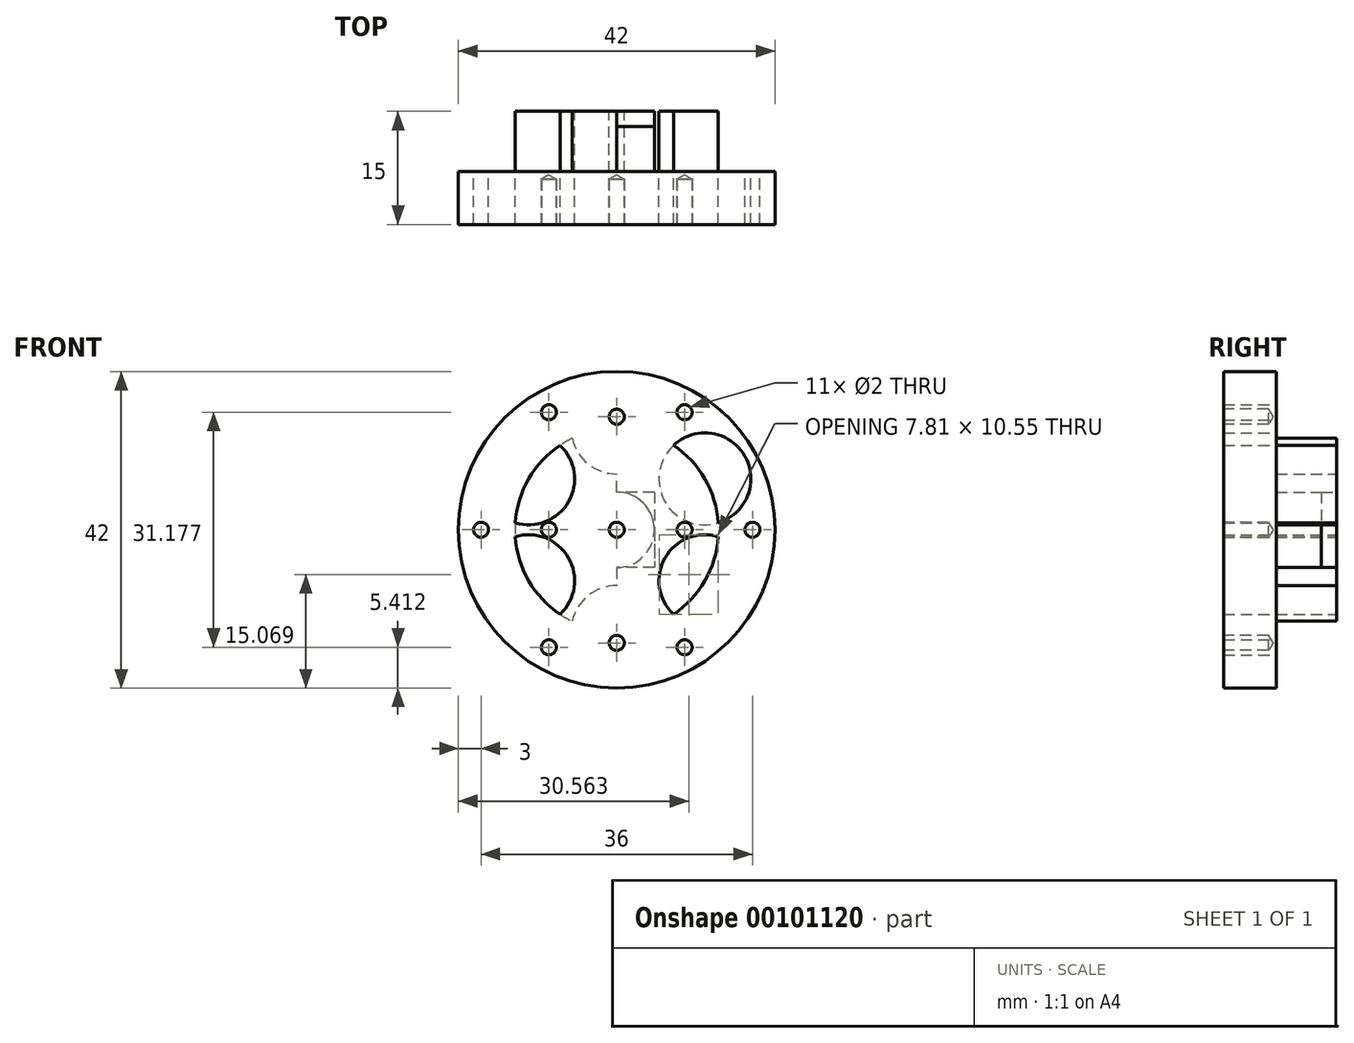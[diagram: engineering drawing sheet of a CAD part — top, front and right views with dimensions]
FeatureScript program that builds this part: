
annotation { "Feature Type Name" : "Feature", "Feature Type Description" : "" }
export const myFeature = defineFeature(function(context is Context, id is Id, definition is map)
    precondition{}
    {
        {
            var Q0;
            Q0=qCreatedBy(makeId("Front.planeOp"),FACE);
            var sketch = newSketch(context, id + "F0", { "sketchPlane" : qUnion([Q0])});
            skCircle(sketch, "E0", {"center": v(0, 0) * mm, "radius": 21 * mm});
            skCircle(sketch, "E1", {"center": v(0, 0) * mm, "radius": 13.5 * mm});
            skCircle(sketch, "E2", {"center": v(0, 13.5) * mm, "radius": 6.1 * mm});
            skLineSegment(sketch, "E3", {"start": v(0, 0) * mm, "end": v(0, 13.5) * mm});
            skLineSegment(sketch, "E4.3.0", {"start": v(0, 0) * mm, "end": v(0, -17.5) * mm});
            skCircle(sketch, "E5", {"center": v(0, 0) * mm, "radius": 5 * mm});
            skCircle(sketch, "E6.1.0", {"center": v(-11.7, 6.75) * mm, "radius": 6.1 * mm});
            skCircle(sketch, "E6.2.0", {"center": v(-11.7, -6.75) * mm, "radius": 6.1 * mm});
            skCircle(sketch, "E6.3.0", {"center": v(0, -13.5) * mm, "radius": 6.1 * mm});
            skCircle(sketch, "E6.4.0", {"center": v(11.7, -6.75) * mm, "radius": 6.1 * mm});
            skCircle(sketch, "E6.5.0", {"center": v(11.7, 6.75) * mm, "radius": 6.1 * mm});
            skSolve(sketch);
        }
        {
            var Q0;
            Q0=qSketchRegion(id+"F0",true);
            var Q1;
            {var subQ3=sQuery(id+"F0.wireOp",EDGE,"tZOFWktZ-ElV9-8rvC-aUia-Pu95TyRWtfmy");var subQ5=sQuery(id+"F0.wireOp",EDGE,"E1");var subQ6=makeQuery(id+"F0.imprint","INTERSECT",VERTEX,{"disambiguationData":[OD(1.0)],"derivedFrom":[subQ5,subQ3]});Q1=makeQuery(id+"F0.imprint","IMPRINT",FACE,{"disambiguationData":[TD([[makeQuery(id+"F0.imprint","IMPRINT",EDGE,{"disambiguationData":[TD([[subQ6,-1.0]])],"derivedFrom":subQ5}),1.0]])]});}
            var Q2;
            {var subQ3=sQuery(id+"F0.wireOp",EDGE,"KCc62wJ9-mbiY-6kxt-bQFC-ecyapfwqHlXu");var subQ5=sQuery(id+"F0.wireOp",EDGE,"E1");var subQ6=makeQuery(id+"F0.imprint","INTERSECT",VERTEX,{"disambiguationData":[OD(1.0)],"derivedFrom":[subQ5,subQ3]});Q2=makeQuery(id+"F0.imprint","IMPRINT",FACE,{"disambiguationData":[TD([[makeQuery(id+"F0.imprint","IMPRINT",EDGE,{"disambiguationData":[TD([[subQ6,-1.0]])],"derivedFrom":subQ5}),1.0]])]});}
            var Q3;
            {var subQ3=sQuery(id+"F0.wireOp",EDGE,"0Yy4USeo-LOO3-cS4v-iVgx-1SsoAEMeRNpn");var subQ5=sQuery(id+"F0.wireOp",EDGE,"E1");var subQ6=makeQuery(id+"F0.imprint","INTERSECT",VERTEX,{"disambiguationData":[OD(1.0)],"derivedFrom":[subQ5,subQ3]});Q3=makeQuery(id+"F0.imprint","IMPRINT",FACE,{"disambiguationData":[TD([[makeQuery(id+"F0.imprint","IMPRINT",EDGE,{"disambiguationData":[TD([[subQ6,-1.0]])],"derivedFrom":subQ5}),1.0]])]});}
            var Q4;
            {var subQ5=sQuery(id+"F0.wireOp",EDGE,"E1");var subQ7=sQuery(id+"F0.wireOp",EDGE,"54YZh0VT-RaSH-f3J3-LX5H-yRfJ3TOlvn7D");var subQ8=makeQuery(id+"F0.imprint","INTERSECT",VERTEX,{"disambiguationData":[OD(0.0)],"derivedFrom":[subQ5,subQ7]});Q4=makeQuery(id+"F0.imprint","IMPRINT",FACE,{"disambiguationData":[TD([[makeQuery(id+"F0.imprint","IMPRINT",EDGE,{"disambiguationData":[TD([[subQ8,-1.0]])],"derivedFrom":subQ5}),1.0]])]});}
            var Q5;
            {var subQ3=sQuery(id+"F0.wireOp",EDGE,"E2");var subQ6=sQuery(id+"F0.wireOp",EDGE,"E1");var subQ9=makeQuery(id+"F0.imprint","INTERSECT",VERTEX,{"disambiguationData":[OD(1.0)],"derivedFrom":[subQ6,subQ3]});Q5=makeQuery(id+"F0.imprint","IMPRINT",FACE,{"disambiguationData":[TD([[makeQuery(id+"F0.imprint","IMPRINT",EDGE,{"disambiguationData":[TD([[subQ9,-1.0]])],"derivedFrom":subQ6}),1.0]])]});}
            var Q6;
            {var subQ0=sQuery(id+"F0.wireOp",EDGE,"E1");var subQ1=makeQuery(id+"F0.imprint","INTERSECT",VERTEX,{"derivedFrom":[subQ0,sQuery(id+"F0.wireOp",EDGE,"E4.3.0")]});Q6=makeQuery(id+"F0.imprint","IMPRINT",FACE,{"disambiguationData":[TD([[makeQuery(id+"F0.imprint","IMPRINT",EDGE,{"disambiguationData":[TD([[subQ1,1.0]])],"derivedFrom":subQ0}),-1.0]])]});}
            var Q7;
            {var subQ0=sQuery(id+"F0.wireOp",EDGE,"E4.3.0");var subQ1=sQuery(id+"F0.wireOp",EDGE,"E1");var subQ2=makeQuery(id+"F0.imprint","INTERSECT",VERTEX,{"derivedFrom":[subQ1,subQ0]});Q7=makeQuery(id+"F0.imprint","IMPRINT",FACE,{"disambiguationData":[TD([[makeQuery(id+"F0.imprint","IMPRINT",EDGE,{"disambiguationData":[TD([[subQ2,-1.0]])],"derivedFrom":subQ1}),1.0]])]});}
            var Q8;
            {var subQ0=sQuery(id+"F0.wireOp",EDGE,"E4.3.0");var subQ1=sQuery(id+"F0.wireOp",EDGE,"E1");var subQ2=makeQuery(id+"F0.imprint","INTERSECT",VERTEX,{"derivedFrom":[subQ1,subQ0]});Q8=makeQuery(id+"F0.imprint","IMPRINT",FACE,{"disambiguationData":[TD([[makeQuery(id+"F0.imprint","IMPRINT",EDGE,{"disambiguationData":[TD([[subQ2,1.0]])],"derivedFrom":subQ1}),1.0]])]});}
            var Q9;
            {var subQ0=sQuery(id+"F0.wireOp",EDGE,"E6.4.0");var subQ1=sQuery(id+"F0.wireOp",EDGE,"E1");var subQ2=makeQuery(id+"F0.imprint","INTERSECT",VERTEX,{"disambiguationData":[OD(0.0)],"derivedFrom":[subQ1,subQ0]});Q9=makeQuery(id+"F0.imprint","IMPRINT",FACE,{"disambiguationData":[TD([[makeQuery(id+"F0.imprint","IMPRINT",EDGE,{"disambiguationData":[TD([[subQ2,-1.0]])],"derivedFrom":subQ1}),-1.0]])]});}
            var Q10;
            {var subQ0=sQuery(id+"F0.wireOp",EDGE,"E6.5.0");var subQ1=sQuery(id+"F0.wireOp",EDGE,"E1");var subQ16=makeQuery(id+"F0.imprint","INTERSECT",VERTEX,{"disambiguationData":[OD(0.0)],"derivedFrom":[subQ1,subQ0]});Q10=makeQuery(id+"F0.imprint","IMPRINT",FACE,{"disambiguationData":[TD([[makeQuery(id+"F0.imprint","IMPRINT",EDGE,{"disambiguationData":[TD([[subQ16,-1.0]])],"derivedFrom":subQ1}),1.0]])]});}
            var Q11;
            {var subQ0=sQuery(id+"F0.wireOp",EDGE,"E4.3.0");var subQ1=sQuery(id+"F0.wireOp",EDGE,"E3");var subQ2=makeQuery(id+"F0.imprint","INTERSECT",VERTEX,{"derivedFrom":[subQ1,subQ0]});Q11=makeQuery(id+"F0.imprint","IMPRINT",FACE,{"disambiguationData":[TD([[makeQuery(id+"F0.imprint","IMPRINT",EDGE,{"disambiguationData":[TD([[subQ2,-1.0]])],"derivedFrom":subQ1}),-1.0]])]});}
            var Q12;
            {var subQ0=sQuery(id+"F0.wireOp",EDGE,"E4.3.0");var subQ1=sQuery(id+"F0.wireOp",EDGE,"E3");var subQ2=makeQuery(id+"F0.imprint","INTERSECT",VERTEX,{"derivedFrom":[subQ1,subQ0]});Q12=makeQuery(id+"F0.imprint","IMPRINT",FACE,{"disambiguationData":[TD([[makeQuery(id+"F0.imprint","IMPRINT",EDGE,{"disambiguationData":[TD([[subQ2,-1.0]])],"derivedFrom":subQ1}),1.0]])]});}
            var Q13;
            {var subQ0=sQuery(id+"F0.wireOp",EDGE,"E6.2.0");var subQ1=sQuery(id+"F0.wireOp",EDGE,"E1");var subQ2=makeQuery(id+"F0.imprint","INTERSECT",VERTEX,{"disambiguationData":[OD(0.0)],"derivedFrom":[subQ1,subQ0]});Q13=makeQuery(id+"F0.imprint","IMPRINT",FACE,{"disambiguationData":[TD([[makeQuery(id+"F0.imprint","IMPRINT",EDGE,{"disambiguationData":[TD([[subQ2,-1.0]])],"derivedFrom":subQ1}),-1.0]])]});}
            var Q14;
            {var subQ0=sQuery(id+"F0.wireOp",EDGE,"E6.1.0");var subQ1=sQuery(id+"F0.wireOp",EDGE,"E1");var subQ2=makeQuery(id+"F0.imprint","INTERSECT",VERTEX,{"disambiguationData":[OD(0.0)],"derivedFrom":[subQ1,subQ0]});Q14=makeQuery(id+"F0.imprint","IMPRINT",FACE,{"disambiguationData":[TD([[makeQuery(id+"F0.imprint","IMPRINT",EDGE,{"disambiguationData":[TD([[subQ2,-1.0]])],"derivedFrom":subQ1}),-1.0]])]});}
            var Q15;
            {var subQ0=sQuery(id+"F0.wireOp",EDGE,"E1");var subQ1=makeQuery(id+"F0.imprint","INTERSECT",VERTEX,{"derivedFrom":[subQ0,sQuery(id+"F0.wireOp",EDGE,"E3")]});Q15=makeQuery(id+"F0.imprint","IMPRINT",FACE,{"disambiguationData":[TD([[makeQuery(id+"F0.imprint","IMPRINT",EDGE,{"disambiguationData":[TD([[subQ1,1.0]])],"derivedFrom":subQ0}),-1.0]])]});}
            var Q16;
            {var subQ0=sQuery(id+"F0.wireOp",EDGE,"E3");var subQ1=sQuery(id+"F0.wireOp",EDGE,"E1");var subQ2=makeQuery(id+"F0.imprint","INTERSECT",VERTEX,{"derivedFrom":[subQ1,subQ0]});Q16=makeQuery(id+"F0.imprint","IMPRINT",FACE,{"disambiguationData":[TD([[makeQuery(id+"F0.imprint","IMPRINT",EDGE,{"disambiguationData":[TD([[subQ2,-1.0]])],"derivedFrom":subQ1}),1.0]])]});}
            var Q17;
            {var subQ0=sQuery(id+"F0.wireOp",EDGE,"E3");var subQ1=sQuery(id+"F0.wireOp",EDGE,"E1");var subQ2=makeQuery(id+"F0.imprint","INTERSECT",VERTEX,{"derivedFrom":[subQ1,subQ0]});Q17=makeQuery(id+"F0.imprint","IMPRINT",FACE,{"disambiguationData":[TD([[makeQuery(id+"F0.imprint","IMPRINT",EDGE,{"disambiguationData":[TD([[subQ2,1.0]])],"derivedFrom":subQ1}),1.0]])]});}
            var Q18;
            {var subQ0=sQuery(id+"F0.wireOp",EDGE,"E6.5.0");var subQ1=sQuery(id+"F0.wireOp",EDGE,"E1");var subQ2=makeQuery(id+"F0.imprint","INTERSECT",VERTEX,{"disambiguationData":[OD(0.0)],"derivedFrom":[subQ1,subQ0]});Q18=makeQuery(id+"F0.imprint","IMPRINT",FACE,{"disambiguationData":[TD([[makeQuery(id+"F0.imprint","IMPRINT",EDGE,{"disambiguationData":[TD([[subQ2,1.0]])],"derivedFrom":subQ1}),1.0]])]});}
            var Q19;
            {var subQ0=sQuery(id+"F0.wireOp",EDGE,"E6.5.0");var subQ1=sQuery(id+"F0.wireOp",EDGE,"E1");var subQ2=makeQuery(id+"F0.imprint","INTERSECT",VERTEX,{"disambiguationData":[OD(0.0)],"derivedFrom":[subQ1,subQ0]});Q19=makeQuery(id+"F0.imprint","IMPRINT",FACE,{"disambiguationData":[TD([[makeQuery(id+"F0.imprint","IMPRINT",EDGE,{"disambiguationData":[TD([[subQ2,1.0]])],"derivedFrom":subQ1}),-1.0]])]});}
            extrude(context, id + "F1", {"entities" : qUnion([Q0, Q1, Q2, Q3, Q4, Q5, Q6, Q7, Q8, Q9, Q10, Q11, Q12, Q13, Q14, Q15, Q16, Q17, Q18, Q19]), "depth" : 15 * mm});
        }
        {
            var Q0;
            {var subQ0=sQuery(id+"F0.wireOp",EDGE,"E6.5.0");var subQ1=sQuery(id+"F0.wireOp",EDGE,"E1");var subQ2=makeQuery(id+"F0.imprint","INTERSECT",VERTEX,{"disambiguationData":[OD(0.0)],"derivedFrom":[subQ1,subQ0]});Q0=makeQuery(id+"F0.imprint","IMPRINT",FACE,{"disambiguationData":[TD([[makeQuery(id+"F0.imprint","IMPRINT",EDGE,{"disambiguationData":[TD([[subQ2,1.0]])],"derivedFrom":subQ1}),1.0]])]});}
            var Q1;
            {var subQ0=sQuery(id+"F0.wireOp",EDGE,"E6.5.0");var subQ1=sQuery(id+"F0.wireOp",EDGE,"E1");var subQ2=makeQuery(id+"F0.imprint","INTERSECT",VERTEX,{"disambiguationData":[OD(0.0)],"derivedFrom":[subQ1,subQ0]});Q1=makeQuery(id+"F0.imprint","IMPRINT",FACE,{"disambiguationData":[TD([[makeQuery(id+"F0.imprint","IMPRINT",EDGE,{"disambiguationData":[TD([[subQ2,1.0]])],"derivedFrom":subQ1}),-1.0]])]});}
            var Q2;
            {var subQ0=sQuery(id+"F0.wireOp",EDGE,"E6.4.0");var subQ1=sQuery(id+"F0.wireOp",EDGE,"E1");var subQ2=makeQuery(id+"F0.imprint","INTERSECT",VERTEX,{"disambiguationData":[OD(0.0)],"derivedFrom":[subQ1,subQ0]});Q2=makeQuery(id+"F0.imprint","IMPRINT",FACE,{"disambiguationData":[TD([[makeQuery(id+"F0.imprint","IMPRINT",EDGE,{"disambiguationData":[TD([[subQ2,-1.0]])],"derivedFrom":subQ1}),-1.0]])]});}
            var Q3;
            {var subQ0=sQuery(id+"F0.wireOp",EDGE,"E6.4.0");var subQ1=sQuery(id+"F0.wireOp",EDGE,"E1");var subQ2=makeQuery(id+"F0.imprint","INTERSECT",VERTEX,{"disambiguationData":[OD(0.0)],"derivedFrom":[subQ1,subQ0]});Q3=makeQuery(id+"F0.imprint","IMPRINT",FACE,{"disambiguationData":[TD([[makeQuery(id+"F0.imprint","IMPRINT",EDGE,{"disambiguationData":[TD([[subQ2,-1.0]])],"derivedFrom":subQ1}),1.0]])]});}
            var Q4;
            {var subQ0=sQuery(id+"F0.wireOp",EDGE,"E4.3.0");var subQ1=sQuery(id+"F0.wireOp",EDGE,"E1");var subQ2=makeQuery(id+"F0.imprint","INTERSECT",VERTEX,{"derivedFrom":[subQ1,subQ0]});Q4=makeQuery(id+"F0.imprint","IMPRINT",FACE,{"disambiguationData":[TD([[makeQuery(id+"F0.imprint","IMPRINT",EDGE,{"disambiguationData":[TD([[subQ2,-1.0]])],"derivedFrom":subQ1}),1.0]])]});}
            var Q5;
            {var subQ0=sQuery(id+"F0.wireOp",EDGE,"E1");var subQ1=makeQuery(id+"F0.imprint","INTERSECT",VERTEX,{"derivedFrom":[subQ0,sQuery(id+"F0.wireOp",EDGE,"E4.3.0")]});Q5=makeQuery(id+"F0.imprint","IMPRINT",FACE,{"disambiguationData":[TD([[makeQuery(id+"F0.imprint","IMPRINT",EDGE,{"disambiguationData":[TD([[subQ1,1.0]])],"derivedFrom":subQ0}),-1.0]])]});}
            var Q6;
            {var subQ0=sQuery(id+"F0.wireOp",EDGE,"E4.3.0");var subQ1=sQuery(id+"F0.wireOp",EDGE,"E1");var subQ2=makeQuery(id+"F0.imprint","INTERSECT",VERTEX,{"derivedFrom":[subQ1,subQ0]});Q6=makeQuery(id+"F0.imprint","IMPRINT",FACE,{"disambiguationData":[TD([[makeQuery(id+"F0.imprint","IMPRINT",EDGE,{"disambiguationData":[TD([[subQ2,1.0]])],"derivedFrom":subQ1}),1.0]])]});}
            var Q7;
            {var subQ0=sQuery(id+"F0.wireOp",EDGE,"E6.2.0");var subQ1=sQuery(id+"F0.wireOp",EDGE,"E1");var subQ2=makeQuery(id+"F0.imprint","INTERSECT",VERTEX,{"disambiguationData":[OD(0.0)],"derivedFrom":[subQ1,subQ0]});Q7=makeQuery(id+"F0.imprint","IMPRINT",FACE,{"disambiguationData":[TD([[makeQuery(id+"F0.imprint","IMPRINT",EDGE,{"disambiguationData":[TD([[subQ2,-1.0]])],"derivedFrom":subQ1}),1.0]])]});}
            var Q8;
            {var subQ0=sQuery(id+"F0.wireOp",EDGE,"E6.2.0");var subQ1=sQuery(id+"F0.wireOp",EDGE,"E1");var subQ2=makeQuery(id+"F0.imprint","INTERSECT",VERTEX,{"disambiguationData":[OD(0.0)],"derivedFrom":[subQ1,subQ0]});Q8=makeQuery(id+"F0.imprint","IMPRINT",FACE,{"disambiguationData":[TD([[makeQuery(id+"F0.imprint","IMPRINT",EDGE,{"disambiguationData":[TD([[subQ2,-1.0]])],"derivedFrom":subQ1}),-1.0]])]});}
            var Q9;
            {var subQ0=sQuery(id+"F0.wireOp",EDGE,"E6.1.0");var subQ1=sQuery(id+"F0.wireOp",EDGE,"E1");var subQ2=makeQuery(id+"F0.imprint","INTERSECT",VERTEX,{"disambiguationData":[OD(0.0)],"derivedFrom":[subQ1,subQ0]});Q9=makeQuery(id+"F0.imprint","IMPRINT",FACE,{"disambiguationData":[TD([[makeQuery(id+"F0.imprint","IMPRINT",EDGE,{"disambiguationData":[TD([[subQ2,-1.0]])],"derivedFrom":subQ1}),1.0]])]});}
            var Q10;
            {var subQ0=sQuery(id+"F0.wireOp",EDGE,"E6.1.0");var subQ1=sQuery(id+"F0.wireOp",EDGE,"E1");var subQ2=makeQuery(id+"F0.imprint","INTERSECT",VERTEX,{"disambiguationData":[OD(0.0)],"derivedFrom":[subQ1,subQ0]});Q10=makeQuery(id+"F0.imprint","IMPRINT",FACE,{"disambiguationData":[TD([[makeQuery(id+"F0.imprint","IMPRINT",EDGE,{"disambiguationData":[TD([[subQ2,-1.0]])],"derivedFrom":subQ1}),-1.0]])]});}
            var Q11;
            {var subQ0=sQuery(id+"F0.wireOp",EDGE,"E3");var subQ1=sQuery(id+"F0.wireOp",EDGE,"E1");var subQ2=makeQuery(id+"F0.imprint","INTERSECT",VERTEX,{"derivedFrom":[subQ1,subQ0]});Q11=makeQuery(id+"F0.imprint","IMPRINT",FACE,{"disambiguationData":[TD([[makeQuery(id+"F0.imprint","IMPRINT",EDGE,{"disambiguationData":[TD([[subQ2,-1.0]])],"derivedFrom":subQ1}),1.0]])]});}
            var Q12;
            {var subQ0=sQuery(id+"F0.wireOp",EDGE,"E3");var subQ1=sQuery(id+"F0.wireOp",EDGE,"E1");var subQ2=makeQuery(id+"F0.imprint","INTERSECT",VERTEX,{"derivedFrom":[subQ1,subQ0]});Q12=makeQuery(id+"F0.imprint","IMPRINT",FACE,{"disambiguationData":[TD([[makeQuery(id+"F0.imprint","IMPRINT",EDGE,{"disambiguationData":[TD([[subQ2,1.0]])],"derivedFrom":subQ1}),1.0]])]});}
            var Q13;
            {var subQ0=sQuery(id+"F0.wireOp",EDGE,"E1");var subQ1=makeQuery(id+"F0.imprint","INTERSECT",VERTEX,{"derivedFrom":[subQ0,sQuery(id+"F0.wireOp",EDGE,"E3")]});Q13=makeQuery(id+"F0.imprint","IMPRINT",FACE,{"disambiguationData":[TD([[makeQuery(id+"F0.imprint","IMPRINT",EDGE,{"disambiguationData":[TD([[subQ1,1.0]])],"derivedFrom":subQ0}),-1.0]])]});}
            extrude(context, id + "F2", {"entities" : qUnion([Q0, Q1, Q2, Q3, Q4, Q5, Q6, Q7, Q8, Q9, Q10, Q11, Q12, Q13]), "operationType" : NewBodyOperationType.REMOVE, "depth" : 8 * mm});
        }
        {
            var Q0;
            Q0=makeQuery(id+"F1.opExtrude","CAP_FACE",FACE,{"disambiguationData":[OSD([sQuery(id+"F0.wireOp",EDGE,"E0")])],"isStart":true});
            var sketch = newSketch(context, id + "F3", { "sketchPlane" : qUnion([Q0])});
            skLineSegment(sketch, "E7.bottom", {"start": v(-5, 5) * mm, "end": v(5, 5) * mm});
            skLineSegment(sketch, "E7.top", {"start": v(-5, -5) * mm, "end": v(5, -5) * mm});
            skLineSegment(sketch, "E7.left", {"start": v(-5, 5) * mm, "end": v(-5, -5) * mm});
            skLineSegment(sketch, "E7.right", {"start": v(5, 5) * mm, "end": v(5, -5) * mm});
            skPoint(sketch, "E7.middle", {"position": v(0, 0) * mm});
            skSolve(sketch);
        }
        {
            var Q0;
            Q0=makeQuery(id+"F1.opExtrude","CAP_FACE",FACE,{"disambiguationData":[OSD([sQuery(id+"F0.wireOp",EDGE,"E0")])],"isStart":false});
            var sketch = newSketch(context, id + "F4", { "sketchPlane" : qUnion([Q0])});
            skLineSegment(sketch, "E8", {"start": v(0, 0) * mm, "end": v(-15, 0) * mm});
            skCircle(sketch, "E9", {"center": v(-15, 0) * mm, "radius": 1.5 * mm});
            skCircle(sketch, "E10.1.0", {"center": v(0, -15) * mm, "radius": 1.5 * mm});
            skCircle(sketch, "E10.2.0", {"center": v(15, 0) * mm, "radius": 1.5 * mm});
            skCircle(sketch, "E10.3.0", {"center": v(0, 15) * mm, "radius": 1.5 * mm});
            skPoint(sketch, "E10.center", {"position": v(0, 0) * mm});
            skSolve(sketch);
        }
        {
            var Q0;
            Q0=makeQuery(id+"F4.imprint","IMPRINT",FACE,{"disambiguationData":[TD([[makeQuery(id+"F4.imprint","IMPRINT",EDGE,{"derivedFrom":sQuery(id+"F4.wireOp",EDGE,"E9")}),-1.0]])]});
            var sketch = newSketch(context, id + "F5", { "sketchPlane" : qUnion([Q0])});
            skPoint(sketch, "E11", {"position": v(0, -9) * mm});
            skPoint(sketch, "E12", {"position": v(0, 9) * mm});
            skPoint(sketch, "E13", {"position": v(-9, 0) * mm});
            skPoint(sketch, "E14", {"position": v(9, 0) * mm});
            skSolve(sketch);
        }
        {
            var Q0;
            Q0=makeQuery(id+"F3.imprint","IMPRINT",FACE,{"disambiguationData":[TD([[makeQuery(id+"F3.imprint","IMPRINT",EDGE,{"derivedFrom":sQuery(id+"F3.wireOp",EDGE,"E7.bottom")}),-1.0]])]});
            extrude(context, id + "F6", {"entities" : qUnion([Q0]), "operationType" : NewBodyOperationType.ADD, "oppositeDirection" : true, "depth" : 2 * mm});
        }
        {
            var Q0;
            Q0=makeQuery(id+"F6.boolean.opBoolean","MERGE",FACE,{"derivedFrom":[makeQuery(id+"F1.opExtrude","CAP_FACE",FACE,{"disambiguationData":[OSD([sQuery(id+"F0.wireOp",EDGE,"E0")])],"isStart":true}),makeQuery(id+"F6.opExtrude","CAP_FACE",FACE,{"disambiguationData":[OSD([sQuery(id+"F3.wireOp",EDGE,"E7.bottom"),sQuery(id+"F3.wireOp",EDGE,"E7.top"),sQuery(id+"F3.wireOp",EDGE,"E7.left"),sQuery(id+"F3.wireOp",EDGE,"E7.right")])],"isStart":true})]});
            var sketch = newSketch(context, id + "F7", { "sketchPlane" : qUnion([Q0])});
            skPoint(sketch, "E15", {"position": v(-18, 0) * mm});
            skPoint(sketch, "E16.1.0", {"position": v(-9, -15.59) * mm});
            skPoint(sketch, "E16.2.0", {"position": v(9, -15.59) * mm});
            skPoint(sketch, "E16.3.0", {"position": v(18, 0) * mm});
            skPoint(sketch, "E16.center", {"position": v(0, 0) * mm});
            skPoint(sketch, "E17.0.4.0", {"position": v(9, 15.59) * mm});
            skPoint(sketch, "E17.0.5.0", {"position": v(-9, 15.59) * mm});
            skSolve(sketch);
        }
        {
            var Q0;
            Q0=sQuery(id+"F7.wireOp",VERTEX,"E15");
            var Q1;
            Q1=sQuery(id+"F7.wireOp",VERTEX,"E16.center");
            var Q2;
            Q2=sQuery(id+"F7.wireOp",VERTEX,"E16.1.0");
            var Q3;
            Q3=sQuery(id+"F7.wireOp",VERTEX,"E16.2.0");
            var Q4;
            Q4=sQuery(id+"F7.wireOp",VERTEX,"E16.3.0");
            var Q5;
            Q5=sQuery(id+"F7.wireOp",VERTEX,"E17.0.4.0");
            var Q6;
            Q6=sQuery(id+"F7.wireOp",VERTEX,"E17.0.5.0");
            var Q7;
            Q7=makeQuery(id+"F1.opExtrude","SWEPT_BODY",BODY,{"disambiguationData":[OSD([sQuery(id+"F0.wireOp",EDGE,"E0")])]});
            hole(context, id + "F8", {"style" : HoleStyle.SIMPLE, "endStyle" : HoleEndStyle.THROUGH, "holeDiameter" : 2 * mm, "locations" : qUnion([Q0, Q1, Q2, Q3, Q4, Q5, Q6]), "scope" : qUnion([Q7]), "isTappedThrough" : true});
        }
        {
            var Q0;
            Q0=sQuery(id+"F5.wireOp",VERTEX,"E13");
            var Q1;
            Q1=sQuery(id+"F5.wireOp",VERTEX,"E14");
            var Q2;
            Q2=sQuery(id+"F4.wireOp",VERTEX,"E10.3.0.center");
            var Q3;
            Q3=sQuery(id+"F4.wireOp",VERTEX,"E10.1.0.center");
            var Q4;
            Q4=makeQuery(id+"F1.opExtrude","SWEPT_BODY",BODY,{"disambiguationData":[OSD([sQuery(id+"F0.wireOp",EDGE,"E0")])]});
            hole(context, id + "F9", {"style" : HoleStyle.SIMPLE, "endStyle" : HoleEndStyle.BLIND, "holeDiameter" : 2 * mm, "holeDepth" : 6 * mm, "locations" : qUnion([Q0, Q1, Q2, Q3]), "scope" : qUnion([Q4])});
        }
    });
